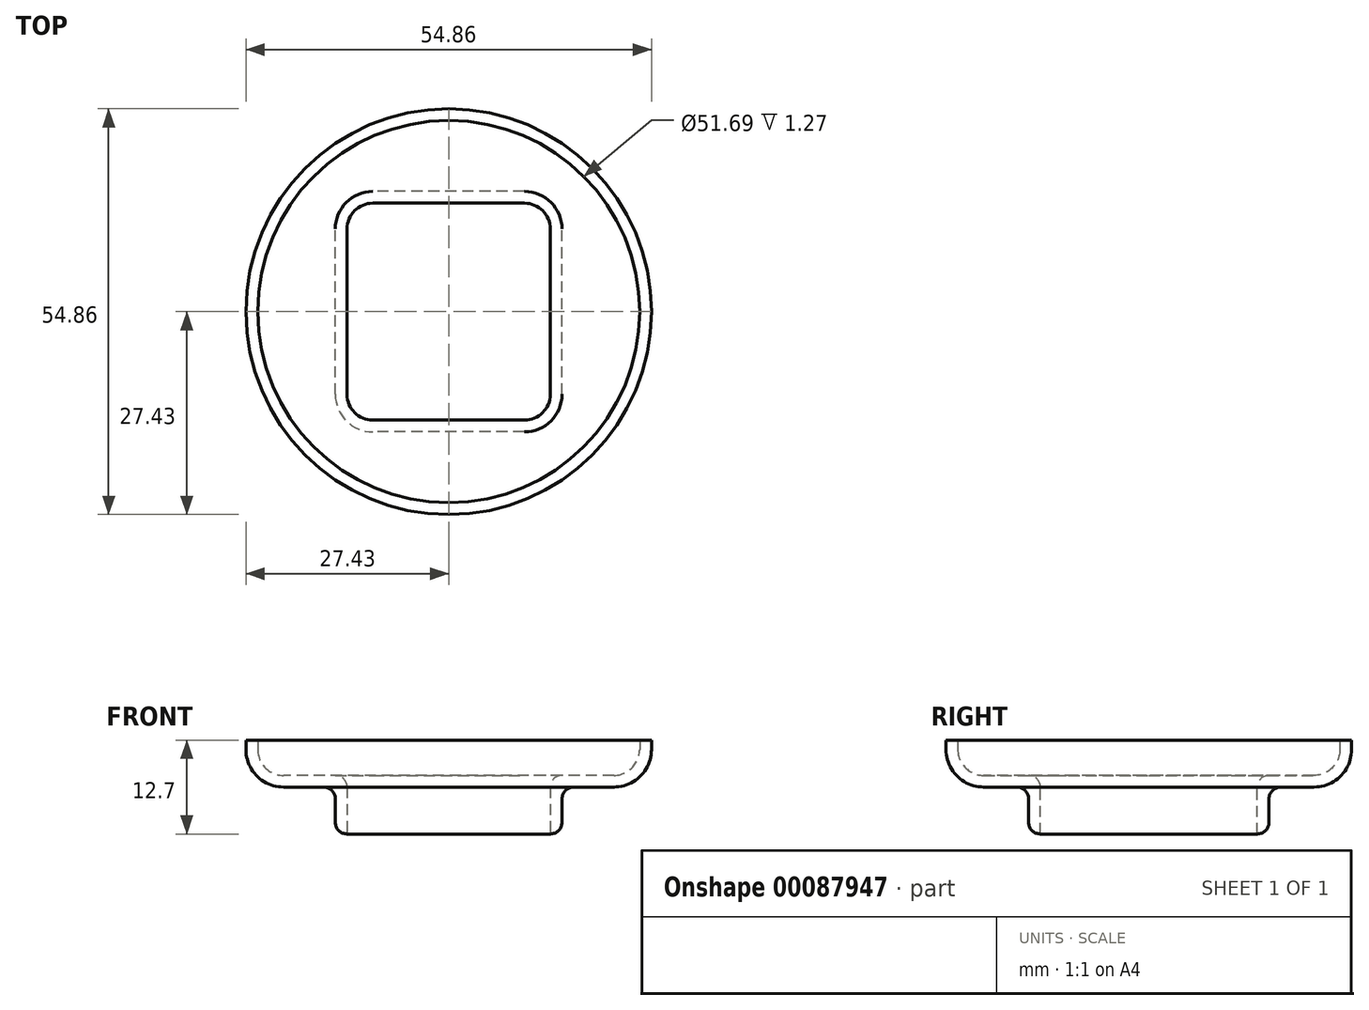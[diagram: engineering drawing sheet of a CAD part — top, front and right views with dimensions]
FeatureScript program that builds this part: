
annotation { "Feature Type Name" : "Feature", "Feature Type Description" : "" }
export const myFeature = defineFeature(function(context is Context, id is Id, definition is map)
    precondition{}
    {
        {
            var Q0;
            Q0=qCreatedBy(makeId("Top.planeOp"),FACE);
            var sketch = newSketch(context, id + "F0", { "sketchPlane" : qUnion([Q0])});
            skCircle(sketch, "E0", {"center": v(0, 0) * mm, "radius": 27.43 * mm});
            skSolve(sketch);
        }
        {
            var Q0;
            Q0=makeQuery(id+"F0.imprint","IMPRINT",FACE,{"disambiguationData":[TD([[makeQuery(id+"F0.imprint","IMPRINT",EDGE,{"derivedFrom":sQuery(id+"F0.wireOp",EDGE,"E0")}),1.0]])]});
            extrude(context, id + "F1", {"entities" : qUnion([Q0]), "depth" : 6.35 * mm});
        }
        {
            var Q0;
            Q0=makeQuery(id+"F1.opExtrude","CAP_EDGE",EDGE,{"disambiguationData":[OSD([sQuery(id+"F0.wireOp",EDGE,"E0")])],"isStart":true});
            fillet(context, id + "F9", {"entities" : qUnion([Q0]), "radius" : 5.08 * mm, "tangentPropagation" : true, "allowEdgeOverflow" : false});
        }
        {
            var Q0;
            Q0=makeQuery(id+"F1.opExtrude","CAP_FACE",FACE,{"disambiguationData":[OSD([sQuery(id+"F0.wireOp",EDGE,"E0")])],"isStart":false});
            shell(context, id + "F2", {"entities" : qUnion([Q0]), "thickness" : 1.59 * mm});
        }
        {
            var Q0;
            Q0=makeQuery(id+"F1.opExtrude","CAP_FACE",FACE,{"disambiguationData":[OSD([sQuery(id+"F0.wireOp",EDGE,"E0")])],"isStart":true});
            var sketch = newSketch(context, id + "F3", { "sketchPlane" : qUnion([Q0])});
            skLineSegment(sketch, "E1.bottom", {"start": v(15.33, 16.26) * mm, "end": v(-15.33, 16.26) * mm});
            skLineSegment(sketch, "E1.top", {"start": v(15.33, -16.26) * mm, "end": v(-15.33, -16.26) * mm});
            skLineSegment(sketch, "E1.left", {"start": v(15.33, 16.26) * mm, "end": v(15.33, -16.26) * mm});
            skLineSegment(sketch, "E1.right", {"start": v(-15.33, 16.26) * mm, "end": v(-15.33, -16.26) * mm});
            skPoint(sketch, "E1.middle", {"position": v(0, 0) * mm});
            skSolve(sketch);
        }
        {
            var Q0;
            Q0=makeQuery(id+"F3.imprint","IMPRINT",FACE,{"disambiguationData":[TD([[makeQuery(id+"F3.imprint","IMPRINT",EDGE,{"derivedFrom":sQuery(id+"F3.wireOp",EDGE,"E1.bottom")}),1.0]])]});
            extrude(context, id + "F4", {"entities" : qUnion([Q0]), "operationType" : NewBodyOperationType.ADD, "depth" : 6.35 * mm});
        }
        {
            var Q0;
            Q0=makeQuery(id+"F4.opExtrude","SWEPT_EDGE",EDGE,{"disambiguationData":[OSD([sQuery(id+"F0.wireOp",EDGE,"E0"),sQuery(id+"F3.wireOp",EDGE,"E1.top"),sQuery(id+"F3.wireOp",EDGE,"E1.right")])]});
            var Q1;
            Q1=makeQuery(id+"F4.opExtrude","SWEPT_EDGE",EDGE,{"disambiguationData":[OSD([sQuery(id+"F0.wireOp",EDGE,"E0"),sQuery(id+"F3.wireOp",EDGE,"E1.bottom"),sQuery(id+"F3.wireOp",EDGE,"E1.right")])]});
            var Q2;
            Q2=makeQuery(id+"F4.opExtrude","SWEPT_EDGE",EDGE,{"disambiguationData":[OSD([sQuery(id+"F0.wireOp",EDGE,"E0"),sQuery(id+"F3.wireOp",EDGE,"E1.bottom"),sQuery(id+"F3.wireOp",EDGE,"E1.left")])]});
            var Q3;
            Q3=makeQuery(id+"F4.opExtrude","SWEPT_EDGE",EDGE,{"disambiguationData":[OSD([sQuery(id+"F0.wireOp",EDGE,"E0"),sQuery(id+"F3.wireOp",EDGE,"E1.top"),sQuery(id+"F3.wireOp",EDGE,"E1.left")])]});
            fillet(context, id + "F5", {"entities" : qUnion([Q0, Q1, Q2, Q3]), "radius" : 5.08 * mm, "tangentPropagation" : true, "allowEdgeOverflow" : false});
        }
        {
            var Q0;
            Q0=makeQuery(id+"F4.opExtrude","CAP_FACE",FACE,{"disambiguationData":[OSD([sQuery(id+"F3.wireOp",EDGE,"E1.bottom"),sQuery(id+"F3.wireOp",EDGE,"E1.top"),sQuery(id+"F3.wireOp",EDGE,"E1.left"),sQuery(id+"F3.wireOp",EDGE,"E1.right")])],"isStart":false});
            shell(context, id + "F6", {"entities" : qUnion([Q0]), "thickness" : 1.59 * mm});
        }
        {
            var Q0;
            Q0=makeQuery(id+"F6.opShell","OFFSET_FACE",FACE,{"disambiguationData":[OSD([sQuery(id+"F0.wireOp",EDGE,"E0")])]});
            extrude(context, id + "F7", {"entities" : qUnion([Q0]), "operationType" : NewBodyOperationType.REMOVE, "endBound" : BoundingType.THROUGH_ALL, "oppositeDirection" : true, "depth" : 25.4 * mm});
        }
        {
            var Q0;
            {var subQ0=sQuery(id+"F0.wireOp",EDGE,"E0");Q0=makeQuery(id+"F7.boolean.opBoolean","INTERSECT",EDGE,{"derivedFrom":[makeQuery(id+"F2.opShell","OFFSET_FACE",FACE,{"disambiguationData":[OSD([subQ0]),TDD([makeQuery(id+"F1.opExtrude","CAP_FACE",FACE,{"disambiguationData":[OSD([subQ0])],"isStart":true})])]}),makeQuery(id+"F7.opExtrude","SWEPT_FACE",FACE,{"disambiguationData":[OSD([subQ0,sQuery(id+"F3.wireOp",EDGE,"E1.left")])]})]});}
            fillet(context, id + "F10", {"entities" : qUnion([Q0]), "radius" : 1.59 * mm, "tangentPropagation" : true, "allowEdgeOverflow" : false});
        }
        {
            var Q0;
            Q0=makeQuery(id+"F4.opExtrude","SWEPT_FACE",FACE,{"disambiguationData":[OSD([sQuery(id+"F3.wireOp",EDGE,"E1.left")])]});
            fillet(context, id + "F11", {"entities" : qUnion([Q0]), "radius" : 1.59 * mm, "tangentPropagation" : true, "allowEdgeOverflow" : false});
        }
    });
